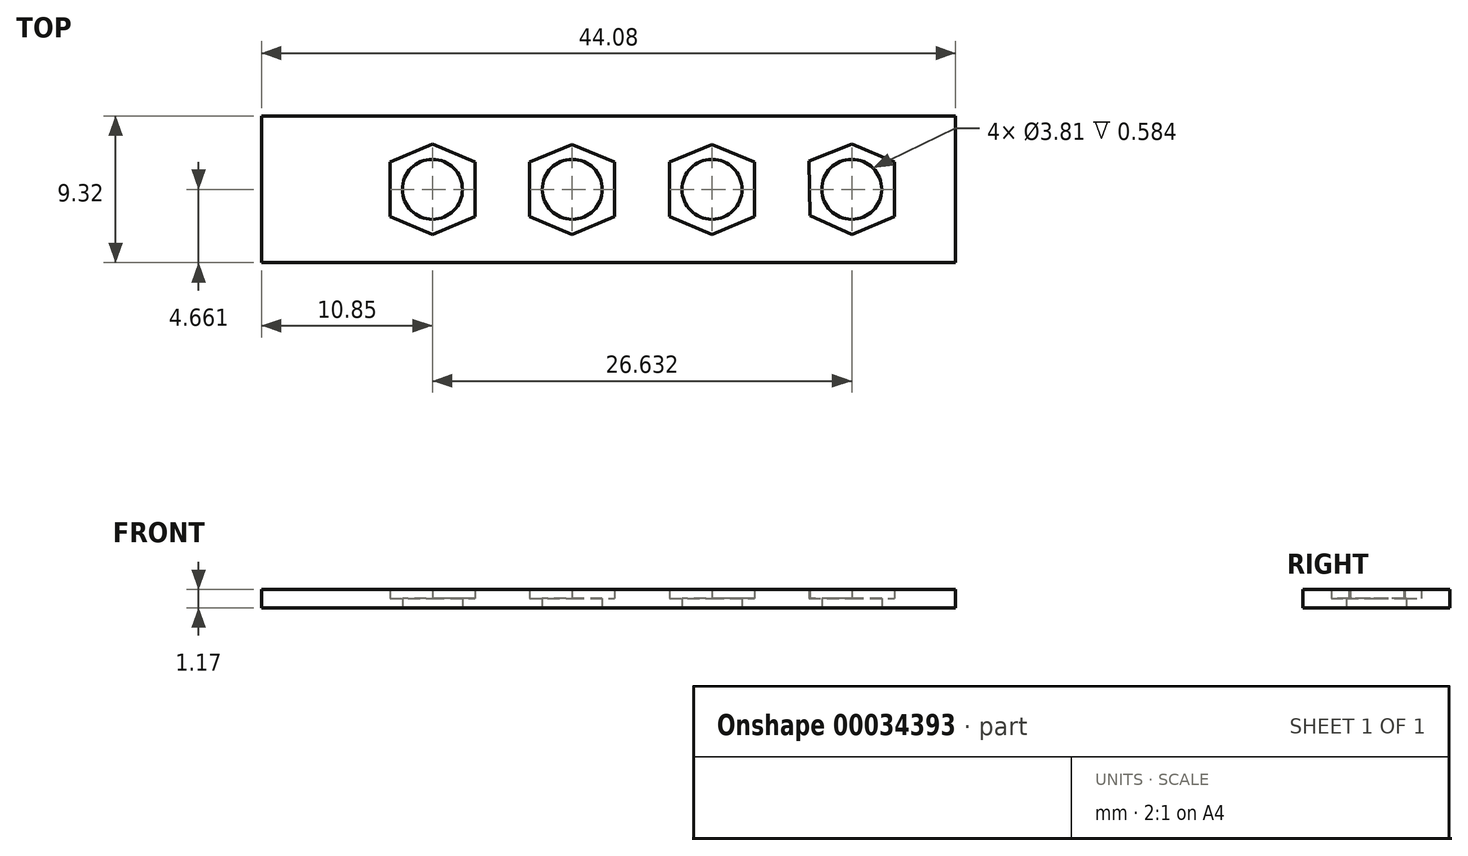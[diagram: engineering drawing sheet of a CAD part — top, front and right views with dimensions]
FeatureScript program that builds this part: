
annotation { "Feature Type Name" : "Feature", "Feature Type Description" : "" }
export const myFeature = defineFeature(function(context is Context, id is Id, definition is map)
    precondition{}
    {
        {
            var Q0;
            Q0=qCreatedBy(makeId("Top.planeOp"),FACE);
            var sketch = newSketch(context, id + "F0", { "sketchPlane" : qUnion([Q0])});
            skLineSegment(sketch, "E0.bottom", {"start": v(0, 0) * mm, "end": v(-44.08, 0) * mm});
            skLineSegment(sketch, "E0.top", {"start": v(0, 9.32) * mm, "end": v(-44.08, 9.32) * mm});
            skLineSegment(sketch, "E0.left", {"start": v(0, 0) * mm, "end": v(0, 9.32) * mm});
            skLineSegment(sketch, "E0.right", {"start": v(-44.08, 0) * mm, "end": v(-44.08, 9.32) * mm});
            skCircle(sketch, "E1", {"center": v(-6.6, 4.66) * mm, "radius": 1.9 * mm});
            skCircle(sketch, "E2", {"center": v(-15.47, 4.66) * mm, "radius": 1.9 * mm});
            skCircle(sketch, "E3", {"center": v(-24.35, 4.66) * mm, "radius": 1.9 * mm});
            skCircle(sketch, "E4", {"center": v(-33.23, 4.66) * mm, "radius": 1.9 * mm});
            skPoint(sketch, "E5", {"position": v(-31.32, 4.66) * mm});
            skPoint(sketch, "E6", {"position": v(-26.26, 4.66) * mm});
            skPoint(sketch, "E7", {"position": v(-22.45, 4.66) * mm});
            skPoint(sketch, "E8", {"position": v(-17.38, 4.66) * mm});
            skPoint(sketch, "E9", {"position": v(-13.57, 4.66) * mm});
            skSolve(sketch);
        }
        {
            var Q0;
            Q0 = qSketchRegion(id + "F0", true);
            extrude(context, id + "F1", {"entities" : qUnion([Q0]), "depth" : 0.58 * mm});
        }
        {
            var Q0;
            Q0=makeQuery(id+"F1.opExtrude","CAP_FACE",FACE,{"disambiguationData":[OSD([sQuery(id+"F0.wireOp",EDGE,"E0.bottom"),sQuery(id+"F0.wireOp",EDGE,"E0.top"),sQuery(id+"F0.wireOp",EDGE,"E0.left"),sQuery(id+"F0.wireOp",EDGE,"E0.right"),sQuery(id+"F0.wireOp",EDGE,"E1"),sQuery(id+"F0.wireOp",EDGE,"E2"),sQuery(id+"F0.wireOp",EDGE,"E3"),sQuery(id+"F0.wireOp",EDGE,"E4")])],"isStart":false});
            var sketch = newSketch(context, id + "F2", { "sketchPlane" : qUnion([Q0])});
            skLineSegment(sketch, "E10", {"start": v(-30.53, 6.4) * mm, "end": v(-30.53, 2.94) * mm});
            skLineSegment(sketch, "E11", {"start": v(-33.23, 4.66) * mm, "end": v(-33.23, 4.66) * mm});
            skLineSegment(sketch, "E12.MirrorCS", {"start": v(-35.93, 6.4) * mm, "end": v(-35.93, 2.94) * mm});
            skLineSegment(sketch, "E13", {"start": v(-33.23, 1.8) * mm, "end": v(-30.53, 2.94) * mm});
            skLineSegment(sketch, "E14", {"start": v(-30.53, 6.4) * mm, "end": v(-33.23, 7.52) * mm});
            skLineSegment(sketch, "E15", {"start": v(-35.93, 6.4) * mm, "end": v(-33.23, 7.52) * mm});
            skLineSegment(sketch, "E16", {"start": v(-35.93, 2.94) * mm, "end": v(-33.23, 1.8) * mm});
            skLineSegment(sketch, "E17.MirrorCS", {"start": v(-27.06, 6.4) * mm, "end": v(-27.06, 2.93) * mm});
            skLineSegment(sketch, "E18", {"start": v(-27.06, 6.4) * mm, "end": v(-24.35, 7.52) * mm});
            skLineSegment(sketch, "E19", {"start": v(-21.65, 6.4) * mm, "end": v(-21.65, 2.93) * mm});
            skLineSegment(sketch, "E20", {"start": v(-21.65, 6.4) * mm, "end": v(-24.35, 7.52) * mm});
            skLineSegment(sketch, "E21", {"start": v(-24.35, 1.79) * mm, "end": v(-21.65, 2.93) * mm});
            skLineSegment(sketch, "E22", {"start": v(-24.35, 1.79) * mm, "end": v(-27.06, 2.93) * mm});
            skLineSegment(sketch, "E23", {"start": v(-15.47, 7.52) * mm, "end": v(-15.47, 7.52) * mm});
            skLineSegment(sketch, "E24.MirrorCS", {"start": v(-18.18, 6.4) * mm, "end": v(-18.18, 2.93) * mm});
            skLineSegment(sketch, "E25", {"start": v(-18.18, 6.4) * mm, "end": v(-15.48, 7.52) * mm});
            skLineSegment(sketch, "E26", {"start": v(-18.18, 2.93) * mm, "end": v(-15.47, 1.8) * mm});
            skLineSegment(sketch, "E27", {"start": v(-15.47, 1.8) * mm, "end": v(-12.78, 2.93) * mm});
            skLineSegment(sketch, "E28", {"start": v(-12.78, 6.4) * mm, "end": v(-12.78, 2.93) * mm});
            skLineSegment(sketch, "E29", {"start": v(-12.78, 6.4) * mm, "end": v(-15.48, 7.52) * mm});
            skLineSegment(sketch, "E30.MirrorCS", {"start": v(-9.32, 6.47) * mm, "end": v(-9.26, 3) * mm});
            skLineSegment(sketch, "E31", {"start": v(-9.32, 6.47) * mm, "end": v(-6.6, 7.52) * mm});
            skLineSegment(sketch, "E32", {"start": v(-3.9, 6.4) * mm, "end": v(-3.9, 2.93) * mm});
            skLineSegment(sketch, "E33", {"start": v(-3.9, 6.4) * mm, "end": v(-6.6, 7.52) * mm});
            skLineSegment(sketch, "E34", {"start": v(-6.6, 1.8) * mm, "end": v(-9.26, 3) * mm});
            skLineSegment(sketch, "E35", {"start": v(-6.6, 1.8) * mm, "end": v(-3.9, 2.93) * mm});
            skPoint(sketch, "E36.end.orphan", {"position": v(-30.53, 4.67) * mm});
            skPoint(sketch, "E37.start.orphan", {"position": v(-24.35, 4.65) * mm});
            skPoint(sketch, "E38.start.orphan", {"position": v(-15.48, 4.66) * mm});
            skPoint(sketch, "E39.orphan", {"position": v(-15.47, 4.66) * mm});
            skPoint(sketch, "E40.start.orphan", {"position": v(-6.6, 4.66) * mm});
            skSolve(sketch);
        }
        {
            var Q0;
            Q0=makeQuery(id+"F2.imprint","IMPRINT",FACE,{"disambiguationData":[TD([[makeQuery(id+"F2.imprint","IMPRINT",EDGE,{"derivedFrom":sQuery(id+"F2.wireOp",EDGE,"E10")}),1.0]])]});
            extrude(context, id + "F3", {"entities" : qUnion([Q0]), "operationType" : NewBodyOperationType.ADD, "depth" : 0.58 * mm});
        }
    });
